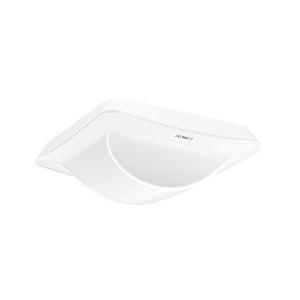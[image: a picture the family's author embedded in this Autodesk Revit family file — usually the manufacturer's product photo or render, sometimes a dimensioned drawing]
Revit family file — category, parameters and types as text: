
# Revit family: hallway_058005
name_source: partatom
category: Elektroinstallationen
revit_build: Autodesk Revit 2016 (Build: 20190508_0715(x64)
units: mm (PartAtom-declared; Revit-internal decimal feet)

## family parameters
Basisbauteil = Fläche
Beim Laden mit Abzugskörper schneiden = Nein
Bemaßung runder Anschluss = Durchmesser verwenden
Beschriftungsausrichtung beibehalten = Nein
Gemeinsam genutzt = Nein
Raumberechnungspunkt = Nein
Teiletyp = Normal

## types (1)
- Hallway
    Apparent Load = 0 VA
    Beschreibung = Type: Presence detector; Dimensions (L x W x H): 67 x 103 x 103 mm; Mains power supply: 220 – 240 V / 50 – 60 Hz; Power consumption: 0,7 W; Sensor Technology: High frequency; Application, place: Indoors; Application, room: Indoors, corridor / aisle; Installation site: ceiling; Installation: Concealed wiring; HF-system: 5,8 GHz; Electronic scalability: Yes; Mechanical scalability: No; Mounting height: 2 – 4 m; Optimum mounting height: 2,8 m; Detection: also through glass, wood and stud walls; Detection angle: 360 °; Angle of aperture: 140 °; Sneak-by guard: Yes; Capability of masking out individual segments: No; Reach, radial: 25 x 3 m (75 m²); Reach, tangential: 25 x 3 m (75 m²); Twilight setting TEACH: Yes; Twilight setting: 2 – 1000 lx; Time setting: 30 sec – 30 min; Switching output 1, resistive: 2000 W; Switching output 1, number of LEDs / fluorescent lamps: 8 pcs.; Switching output 1, floating: No; Switching output 2, resistive: 230 W; Switching output 2, floating: Yes; Constant-lighting control: No; Basic light level function: No; Functions: Group parameterisation, Semi-/fully automatic, Lighting scenario, Manual ON / ON-OFF, Neighbouring-group function, Normal / test mode; Settings via: Bluetooth; With remote control: No; Interconnection: Yes; IP-rating: IP20; Material: Plastic; Ambient temperature: -20 – 50 °C; Colour: white; Colour, RAL: 9003; Manufacturer's Warranty: 5 years; Version: COM2 - Concealed wiring; PU1, EAN: 4007841058005
    Height = 0 mm  [stored 0 ft]
    Hersteller = Steinel
    Length = 67 mm
    Maximum range = 10.635 m
    ModVariant = Nein
    Modell = 058005
    Mounting Place = Ceiling
    Mounting Type = Recessed
    Number of Poles = 1
    OnlyDefault = Ja
    Power Factor = 1
    Product Name = Hallway
    Product group = Presence detector
    ProductGroupID = 4
    Protection Class = Protection class
    Protection Degree = IP 20
    RlxData = <blob elided: 186773 chars, md5=48b8884e>
    Sensor characteristics = Stretched
    Sensor type = HF
    SensorDataFile = <blob elided: 184606 chars, md5=d44d1097>
    Type of entry = Motion
    Typenbild = produkt1_058005.jpg
    Typenkommentare = Product without accessories
    URL = http://relux.com
    VarID = ---
    Voltage = 0 V
    Vorgabe-Ansicht = 1800 mm
    Weight = 0.00 kg
    Width = 103 mm

note: [stored X ft] marks values corroborated as IEEE doubles in the binary element streams (Revit-internal decimal feet)

## geometry (parser evidence)
native form markers: Blend x4, Sweep x16
no freeform markers — native parametric forms only
